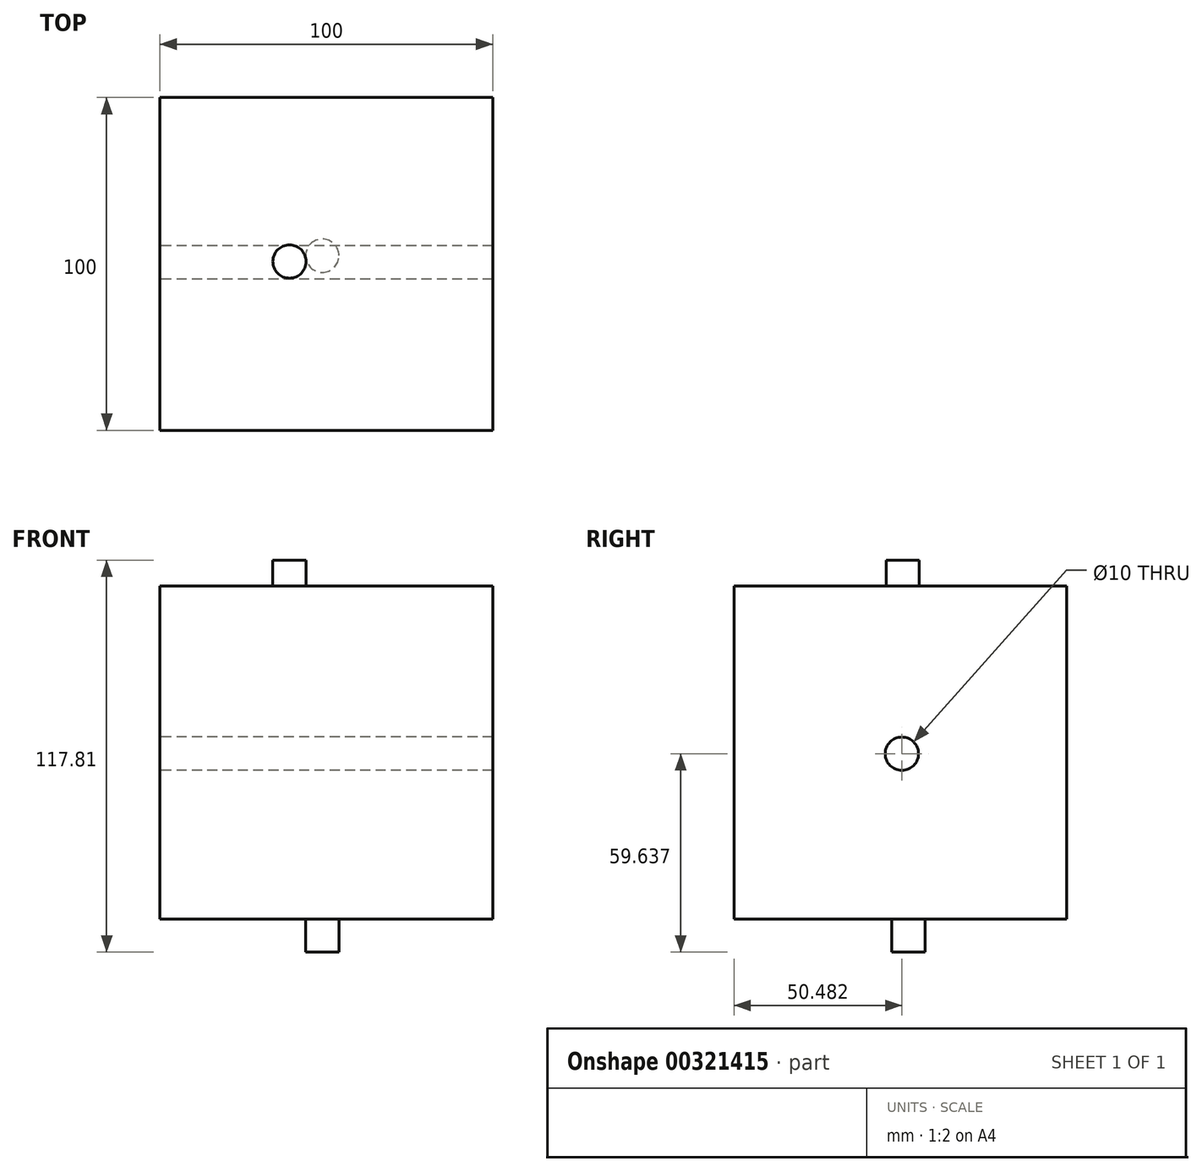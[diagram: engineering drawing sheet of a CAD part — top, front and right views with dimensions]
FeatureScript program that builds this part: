
annotation { "Feature Type Name" : "Feature", "Feature Type Description" : "" }
export const myFeature = defineFeature(function(context is Context, id is Id, definition is map)
    precondition{}
    {
        {
            var Q0;
            Q0=qCreatedBy(makeId("Front.planeOp"),FACE);
            var sketch = newSketch(context, id + "F0", { "sketchPlane" : qUnion([Q0])});
            skLineSegment(sketch, "E0.bottom", {"start": v(0, 0) * mm, "end": v(100, 0) * mm});
            skLineSegment(sketch, "E0.top", {"start": v(0, 100) * mm, "end": v(100, 100) * mm});
            skLineSegment(sketch, "E0.left", {"start": v(0, 0) * mm, "end": v(0, 100) * mm});
            skLineSegment(sketch, "E0.right", {"start": v(100, 0) * mm, "end": v(100, 100) * mm});
            skSolve(sketch);
        }
        {
            var Q0;
            Q0 = qSketchRegion(id + "F0", true);
            extrude(context, id + "F1", {"entities" : qUnion([Q0]), "depth" : 100 * mm});
        }
        {
            var Q0;
            Q0=qCreatedBy(makeId("Top.planeOp"),FACE);
            var sketch = newSketch(context, id + "F2", { "sketchPlane" : qUnion([Q0])});
            skCircle(sketch, "E1", {"center": v(48.76, -47.52) * mm, "radius": 5 * mm});
            skSolve(sketch);
        }
        {
            var Q0;
            Q0 = qSketchRegion(id + "F2", true);
            extrude(context, id + "F3", {"entities" : qUnion([Q0]), "operationType" : NewBodyOperationType.ADD, "oppositeDirection" : true, "depth" : 10 * mm});
        }
        {
            var Q0;
            Q0=qCreatedBy(makeId("Top.planeOp"),FACE);
            var sketch = newSketch(context, id + "F4", { "sketchPlane" : qUnion([Q0])});
            skCircle(sketch, "E2", {"center": v(38.91, -49.28) * mm, "radius": 5 * mm});
            skSolve(sketch);
        }
        {
            var Q0;
            Q0 = qSketchRegion(id + "F4", true);
            extrude(context, id + "F5", {"entities" : qUnion([Q0]), "operationType" : NewBodyOperationType.ADD, "depth" : 107.8 * mm});
        }
        {
            var Q0;
            Q0=qCreatedBy(makeId("Right.planeOp"),FACE);
            var sketch = newSketch(context, id + "F6", { "sketchPlane" : qUnion([Q0])});
            skCircle(sketch, "E3", {"center": v(-49.52, 49.64) * mm, "radius": 5 * mm});
            skSolve(sketch);
        }
        {
            var Q0;
            Q0 = qSketchRegion(id + "F6", true);
            extrude(context, id + "F7", {"entities" : qUnion([Q0]), "operationType" : NewBodyOperationType.REMOVE, "depth" : 333.94 * mm});
        }
    });
